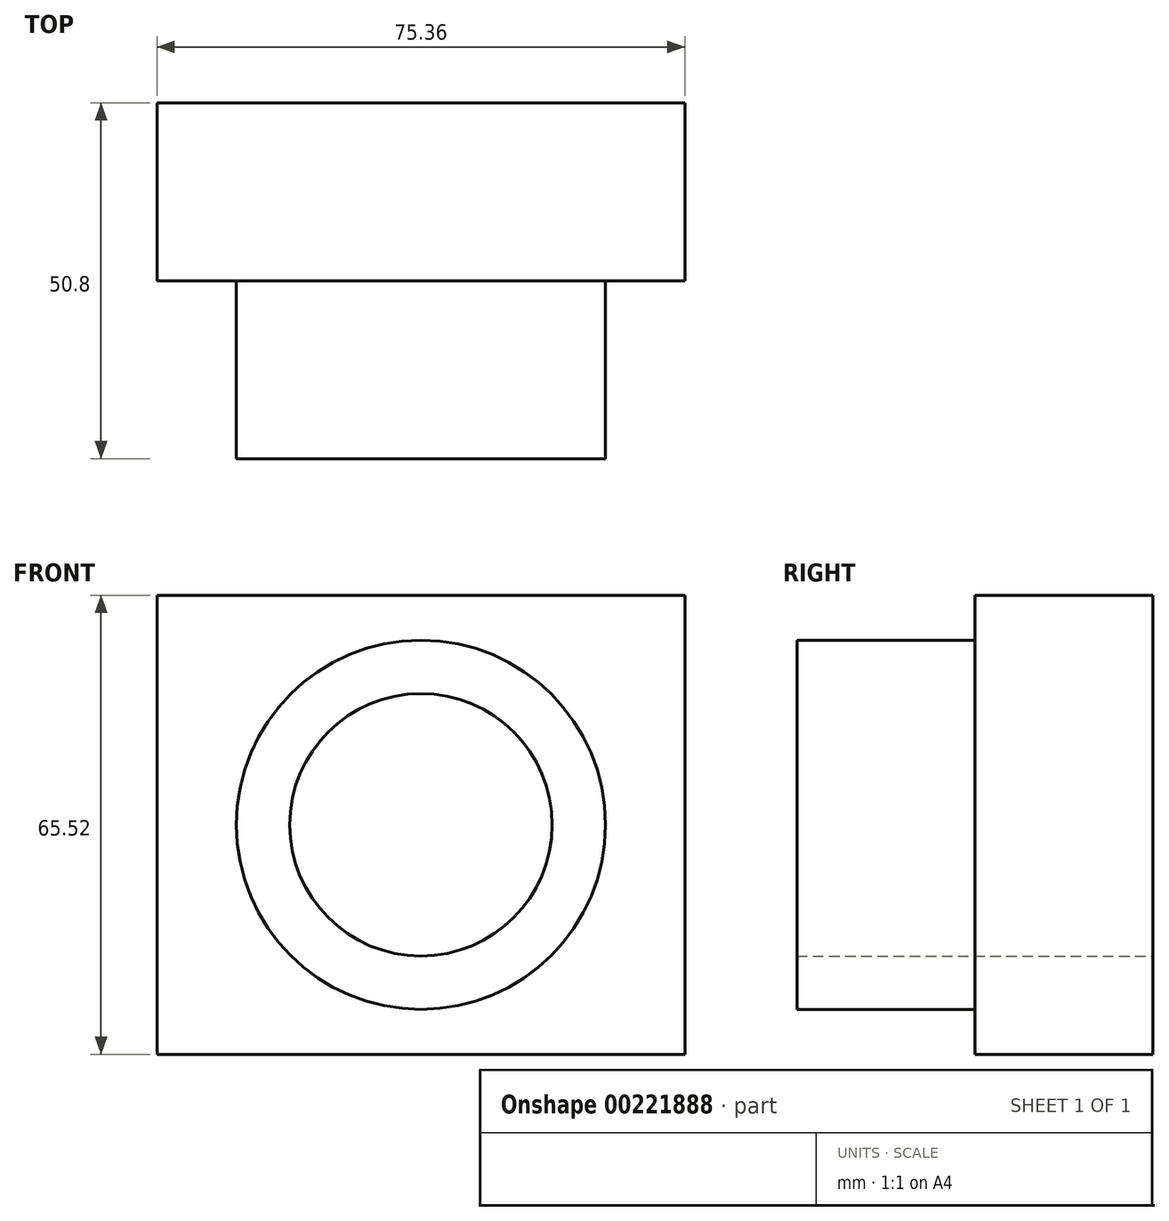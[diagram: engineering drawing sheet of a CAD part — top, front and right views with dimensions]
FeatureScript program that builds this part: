
annotation { "Feature Type Name" : "Feature", "Feature Type Description" : "" }
export const myFeature = defineFeature(function(context is Context, id is Id, definition is map)
    precondition{}
    {
        {
            var Q0;
            Q0=qCreatedBy(makeId("Front.planeOp"),FACE);
            var sketch = newSketch(context, id + "F0", { "sketchPlane" : qUnion([Q0])});
            skLineSegment(sketch, "E0.bottom", {"start": v(-37.68, 32.76) * mm, "end": v(37.68, 32.76) * mm});
            skLineSegment(sketch, "E0.top", {"start": v(-37.68, -32.76) * mm, "end": v(37.68, -32.76) * mm});
            skLineSegment(sketch, "E0.left", {"start": v(-37.68, 32.76) * mm, "end": v(-37.68, -32.76) * mm});
            skLineSegment(sketch, "E0.right", {"start": v(37.68, 32.76) * mm, "end": v(37.68, -32.76) * mm});
            skPoint(sketch, "E0.middle", {"position": v(0, 0) * mm});
            skSolve(sketch);
        }
        {
            var Q0;
            Q0 = qSketchRegion(id + "F0", true);
            extrude(context, id + "F1", {"entities" : qUnion([Q0]), "oppositeDirection" : true, "depth" : 25.4 * mm});
        }
        {
            var Q0;
            Q0=qCreatedBy(makeId("Front.planeOp"),FACE);
            var sketch = newSketch(context, id + "F2", { "sketchPlane" : qUnion([Q0])});
            skCircle(sketch, "E1", {"center": v(0, 0) * mm, "radius": 26.35 * mm});
            skSolve(sketch);
        }
        {
            var Q0;
            Q0 = qSketchRegion(id + "F2", true);
            extrude(context, id + "F3", {"entities" : qUnion([Q0]), "operationType" : NewBodyOperationType.ADD, "depth" : 25.4 * mm});
        }
        {
            var Q0;
            Q0=qCreatedBy(makeId("Front.planeOp"),FACE);
            var sketch = newSketch(context, id + "F4", { "sketchPlane" : qUnion([Q0])});
            skCircle(sketch, "E2", {"center": v(0, 0) * mm, "radius": 18.73 * mm});
            skSolve(sketch);
        }
        {
            var Q0;
            Q0 = qSketchRegion(id + "F4", true);
            extrude(context, id + "F5", {"entities" : qUnion([Q0]), "operationType" : NewBodyOperationType.REMOVE, "endBound" : BoundingType.THROUGH_ALL, "depth" : 254 * mm});
        }
        {
            var Q0;
            Q0 = qSketchRegion(id + "F4", true);
            extrude(context, id + "F6", {"entities" : qUnion([Q0]), "operationType" : NewBodyOperationType.REMOVE, "endBound" : BoundingType.THROUGH_ALL, "oppositeDirection" : true, "depth" : 101.6 * mm});
        }
    });
